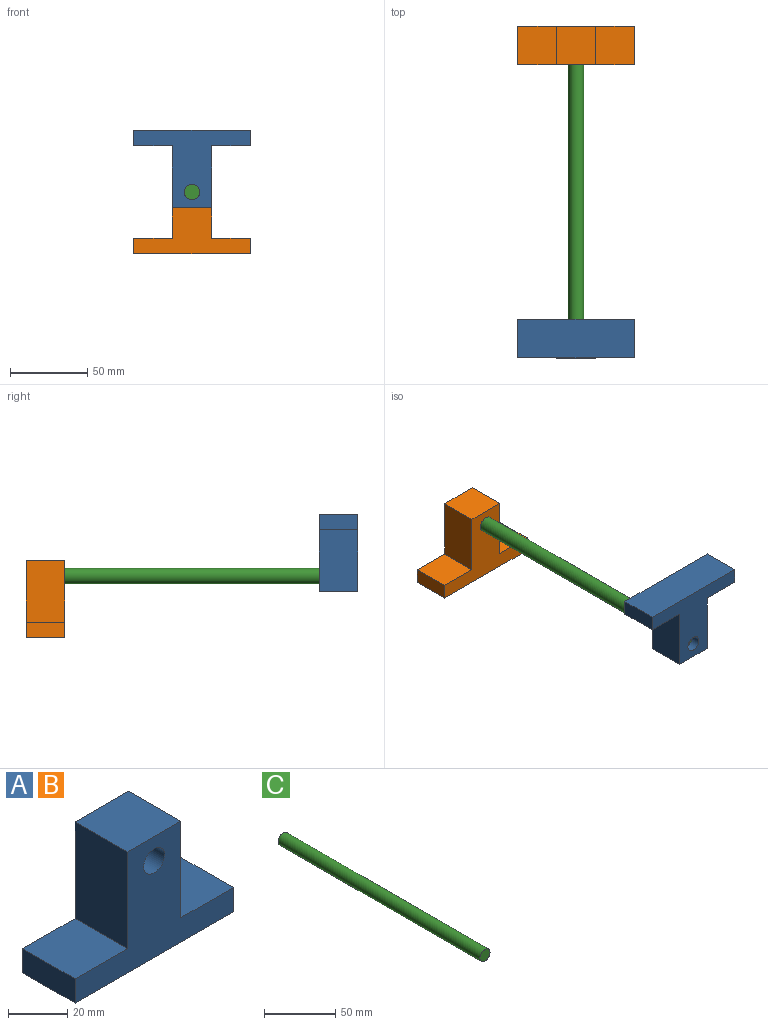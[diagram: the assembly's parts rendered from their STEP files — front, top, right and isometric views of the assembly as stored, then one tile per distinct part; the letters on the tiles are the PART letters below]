
ASSEMBLY  parts=3 mates=2
PART A: 11 faces, bbox 75.6x25x50 mm
  f0: plane 25x25mm, normal (0,0,1), area 625mm2, adj f1,f7,f8,f9
  f1: plane 40x25mm, normal (1,0,0), area 1000mm2, adj f0,f2,f8,f9
  f2: plane 25.65x25mm, normal (0,0,1), area 641.1mm2, adj f1,f3,f8,f9
  f3: plane 40x25mm, normal (-1,0,0), area 1000mm2, adj f2,f4,f8,f9
  f4: plane 25x25mm, normal (0,0,1), area 625mm2, adj f3,f5,f8,f9
  f5: plane 25x10mm, normal (-1,0,0), area 250mm2, adj f4,f6,f8,f9
  f6: plane 75.65x25mm, normal (0,0,-1), area 1891.1mm2, adj f5,f7,f8,f9
  f7: plane 25x10mm, normal (1,0,0), area 250mm2, adj f0,f6,f8,f9
  f8: plane 75.65x50mm, normal (0,-1,0), area 1703.7mm2, adj f0,f1,f2,f3,f4,f5,f6,f7
  f9: plane 75.65x50mm, normal (0,1,0), area 1703.7mm2, adj f0,f1,f2,f3,f4,f5,f6,f7
  f10: cylinder r=5mm len=25mm, axis (0,-1,0), area 785.4mm2, adj f8,f9
PART B: same geometry as A
PART C: 3 faces, bbox 10x200x10 mm
  f0: cylinder r=5mm len=200mm, axis (0,1,0), area 6283.2mm2, adj f1,f2
  f1: plane 10x10mm, normal (0,-1,0), area 78.5mm2, adj f0
  f2: plane 10x10mm, normal (0,1,0), area 78.5mm2, adj f0
PLACE A rot(axis=(1,0,0),180deg) t=(-26.06,-50,-12.49)mm
PLACE B t=(-26.06,165.47,-42.49)mm
PLACE C rot(axis=(1,0,0),180deg) t=(-26.06,-44.03,-27.49)mm
MATE slider C.f0 <-> A.f10  axis (0,-1,0) through (-26.06,155.97,-27.49)mm
MATE slider C.f0 <-> B.f10  axis (0,-1,0) through (-26.06,55.97,-27.49)mm
